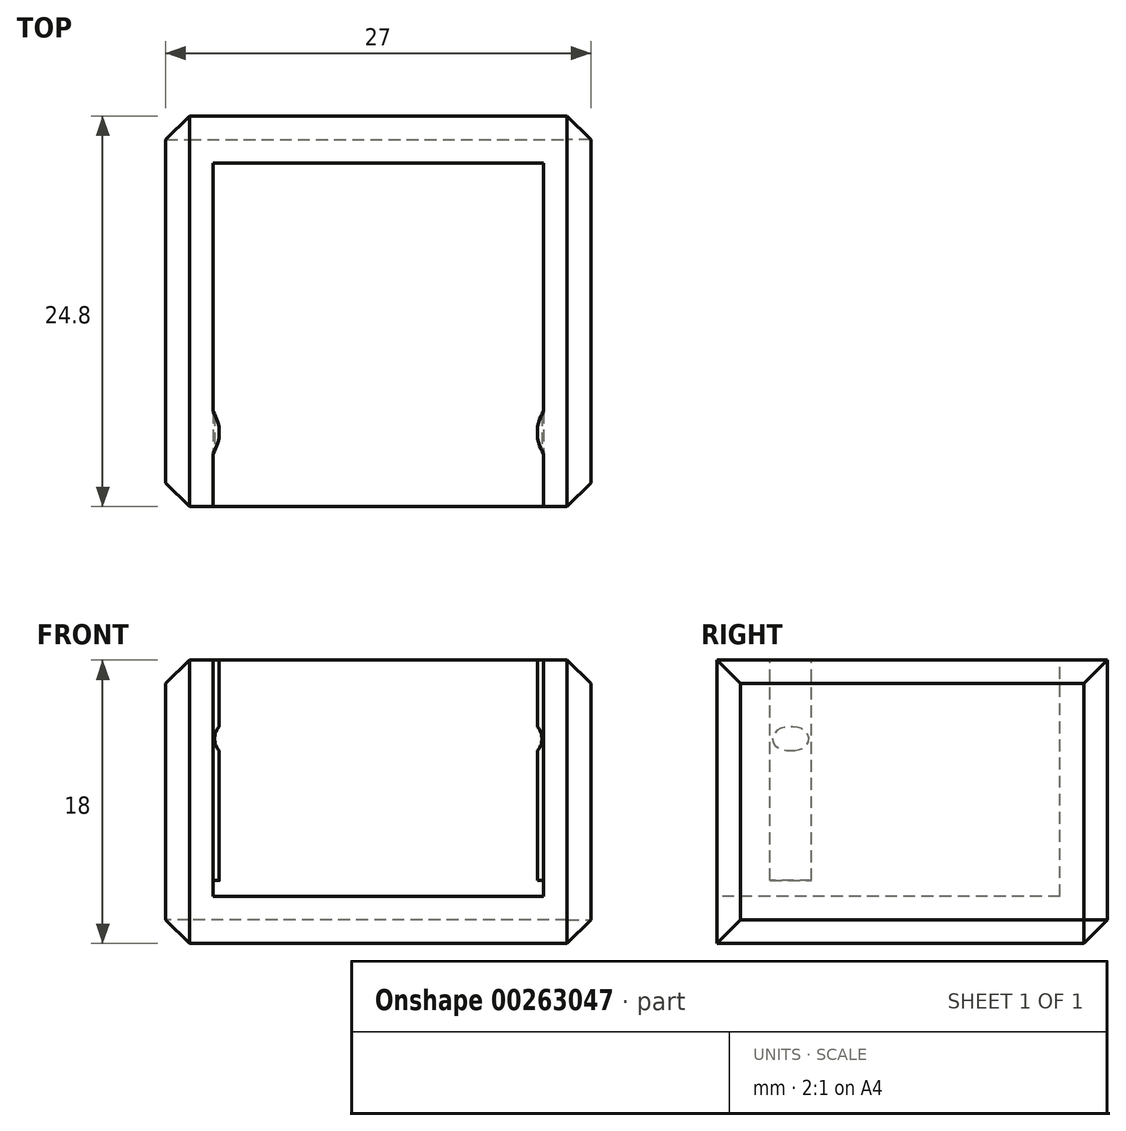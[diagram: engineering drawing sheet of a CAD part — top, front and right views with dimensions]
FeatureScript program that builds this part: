
annotation { "Feature Type Name" : "Feature", "Feature Type Description" : "" }
export const myFeature = defineFeature(function(context is Context, id is Id, definition is map)
    precondition{}
    {
        {
            var Q0;
            Q0=qCreatedBy(makeId("Top.planeOp"),FACE);
            var sketch = newSketch(context, id + "F0", { "sketchPlane" : qUnion([Q0])});
            skLineSegment(sketch, "E0.bottom", {"start": v(13.5, 12.4) * mm, "end": v(-13.5, 12.4) * mm});
            skLineSegment(sketch, "E0.top", {"start": v(13.5, -12.4) * mm, "end": v(-13.5, -12.4) * mm});
            skLineSegment(sketch, "E0.left", {"start": v(13.5, 12.4) * mm, "end": v(13.5, -12.4) * mm});
            skLineSegment(sketch, "E0.right", {"start": v(-13.5, 12.4) * mm, "end": v(-13.5, -12.4) * mm});
            skPoint(sketch, "E0.middle", {"position": v(0, 0) * mm});
            skSolve(sketch);
        }
        {
            var Q0;
            Q0=makeQuery(id+"F0.imprint","IMPRINT",FACE,{"disambiguationData":[TD([[makeQuery(id+"F0.imprint","IMPRINT",EDGE,{"derivedFrom":sQuery(id+"F0.wireOp",EDGE,"E0.bottom")}),1.0]])]});
            extrude(context, id + "F1", {"entities" : qUnion([Q0]), "depth" : 18 * mm});
        }
        {
            var Q0;
            Q0=makeQuery(id+"F1.opExtrude","CAP_FACE",FACE,{"disambiguationData":[OSD([sQuery(id+"F0.wireOp",EDGE,"E0.bottom"),sQuery(id+"F0.wireOp",EDGE,"E0.top"),sQuery(id+"F0.wireOp",EDGE,"E0.left"),sQuery(id+"F0.wireOp",EDGE,"E0.right")])],"isStart":false});
            var sketch = newSketch(context, id + "F2", { "sketchPlane" : qUnion([Q0])});
            skLineSegment(sketch, "E1.bottom", {"start": v(10.5, 9.4) * mm, "end": v(-10.5, 9.4) * mm});
            skLineSegment(sketch, "E1.top", {"start": v(10.5, -12.4) * mm, "end": v(-10.5, -12.4) * mm});
            skLineSegment(sketch, "E1.left", {"start": v(10.5, 9.4) * mm, "end": v(10.5, -12.4) * mm});
            skLineSegment(sketch, "E1.right", {"start": v(-10.5, 9.4) * mm, "end": v(-10.5, -12.4) * mm});
            skPoint(sketch, "E1.middle", {"position": v(0, -1.5) * mm});
            skLineSegment(sketch, "E2", {"start": v(13.5, -12.4) * mm, "end": v(-13.5, -12.4) * mm, "construction": true});
            skLineSegment(sketch, "E3", {"start": v(0, -12.4) * mm, "end": v(0, -1.5) * mm, "construction": true});
            skSolve(sketch);
        }
        {
            var Q0;
            Q0=makeQuery(id+"F2.imprint","IMPRINT",FACE,{"disambiguationData":[TD([[makeQuery(id+"F2.imprint","IMPRINT",EDGE,{"derivedFrom":sQuery(id+"F2.wireOp",EDGE,"E1.bottom")}),1.0]])]});
            extrude(context, id + "F3", {"entities" : qUnion([Q0]), "operationType" : NewBodyOperationType.REMOVE, "oppositeDirection" : true, "depth" : 15 * mm});
        }
        {
            var Q0;
            Q0=makeQuery(id+"F1.opExtrude","CAP_FACE",FACE,{"disambiguationData":[OSD([sQuery(id+"F0.wireOp",EDGE,"E0.bottom"),sQuery(id+"F0.wireOp",EDGE,"E0.top"),sQuery(id+"F0.wireOp",EDGE,"E0.left"),sQuery(id+"F0.wireOp",EDGE,"E0.right")])],"isStart":false});
            var sketch = newSketch(context, id + "F4", { "sketchPlane" : qUnion([Q0])});
            skLineSegment(sketch, "E4", {"start": v(-10.5, 12.4) * mm, "end": v(-10.5, -7.7) * mm, "construction": true});
            skLineSegment(sketch, "E5", {"start": v(-10.5, -7.7) * mm, "end": v(-12.5, -7.7) * mm, "construction": true});
            skArc(sketch, "E6", {"start": v(-10.5, -6.37) * mm, "mid": v(-10.1, -7.7) * mm, "end": v(-10.5, -9.03) * mm});
            skLineSegment(sketch, "E7", {"start": v(0, 0) * mm, "end": v(0, 12.4) * mm, "construction": true});
            skLineSegment(sketch, "E8", {"start": v(-10.5, -9.03) * mm, "end": v(-10.5, -6.37) * mm});
            skLineSegment(sketch, "E9.MirrorCS", {"start": v(10.5, -9.03) * mm, "end": v(10.5, -6.37) * mm});
            skArc(sketch, "E10.MirrorCS", {"start": v(10.5, -6.37) * mm, "mid": v(10.1, -7.7) * mm, "end": v(10.5, -9.03) * mm});
            skSolve(sketch);
        }
        {
            var Q0;
            Q0 = qSketchRegion(id + "F4", true);
            extrude(context, id + "F5", {"entities" : qUnion([Q0]), "operationType" : NewBodyOperationType.ADD, "oppositeDirection" : true, "depth" : 14 * mm});
        }
        {
            var Q0;
            Q0=makeQuery(id+"F1.opExtrude","SWEPT_FACE",FACE,{"disambiguationData":[OSD([sQuery(id+"F0.wireOp",EDGE,"E0.top")])]});
            var sketch = newSketch(context, id + "F6", { "sketchPlane" : qUnion([Q0])});
            skLineSegment(sketch, "E11", {"start": v(10.5, 18) * mm, "end": v(10.5, 13) * mm, "construction": true});
            skLineSegment(sketch, "E12", {"start": v(10.5, 13) * mm, "end": v(9.3, 13) * mm, "construction": true});
            skArc(sketch, "E13", {"start": v(10, 13.85) * mm, "mid": v(10.4, 13) * mm, "end": v(10, 12.15) * mm});
            skLineSegment(sketch, "E14", {"start": v(10, 12.15) * mm, "end": v(10, 13.85) * mm});
            skLineSegment(sketch, "E15", {"start": v(0, 0) * mm, "end": v(0, 18) * mm, "construction": true});
            skArc(sketch, "E16.MirrorCS", {"start": v(-10, 13.85) * mm, "mid": v(-10.4, 13) * mm, "end": v(-10, 12.15) * mm});
            skLineSegment(sketch, "E17.MirrorCS", {"start": v(-10, 12.15) * mm, "end": v(-10, 13.85) * mm});
            skSolve(sketch);
        }
        {
            var Q0;
            Q0 = qSketchRegion(id + "F6", true);
            extrude(context, id + "F7", {"entities" : qUnion([Q0]), "operationType" : NewBodyOperationType.REMOVE, "oppositeDirection" : true, "depth" : 10 * mm});
        }
        {
            var Q0;
            Q0=makeQuery(id+"F1.opExtrude","CAP_EDGE",EDGE,{"disambiguationData":[OSD([sQuery(id+"F0.wireOp",EDGE,"E0.left")])],"isStart":true});
            var Q1;
            Q1=makeQuery(id+"F1.opExtrude","CAP_EDGE",EDGE,{"disambiguationData":[OSD([sQuery(id+"F0.wireOp",EDGE,"E0.left")])],"isStart":false});
            var Q2;
            Q2=makeQuery(id+"F1.opExtrude","CAP_EDGE",EDGE,{"disambiguationData":[OSD([sQuery(id+"F0.wireOp",EDGE,"E0.right")])],"isStart":false});
            var Q3;
            Q3=makeQuery(id+"F1.opExtrude","CAP_EDGE",EDGE,{"disambiguationData":[OSD([sQuery(id+"F0.wireOp",EDGE,"E0.right")])],"isStart":true});
            var Q4;
            Q4=makeQuery(id+"F1.opExtrude","SWEPT_EDGE",EDGE,{"disambiguationData":[OSD([sQuery(id+"F0.wireOp",EDGE,"E0.bottom"),sQuery(id+"F0.wireOp",EDGE,"E0.right")])]});
            var Q5;
            Q5=makeQuery(id+"F1.opExtrude","CAP_EDGE",EDGE,{"disambiguationData":[OSD([sQuery(id+"F0.wireOp",EDGE,"E0.bottom")])],"isStart":true});
            var Q6;
            Q6=makeQuery(id+"F1.opExtrude","SWEPT_EDGE",EDGE,{"disambiguationData":[OSD([sQuery(id+"F0.wireOp",EDGE,"E0.top"),sQuery(id+"F0.wireOp",EDGE,"E0.left")])]});
            var Q7;
            Q7=makeQuery(id+"F1.opExtrude","SWEPT_EDGE",EDGE,{"disambiguationData":[OSD([sQuery(id+"F0.wireOp",EDGE,"E0.top"),sQuery(id+"F0.wireOp",EDGE,"E0.right")])]});
            var Q8;
            Q8=makeQuery(id+"F1.opExtrude","SWEPT_EDGE",EDGE,{"disambiguationData":[OSD([sQuery(id+"F0.wireOp",EDGE,"E0.bottom"),sQuery(id+"F0.wireOp",EDGE,"E0.left")])]});
            chamfer(context, id + "F8", {"entities" : qUnion([Q0, Q1, Q2, Q3, Q4, Q5, Q6, Q7, Q8]), "width" : 1.5 * mm, "tangentPropagation" : true});
        }
    });
